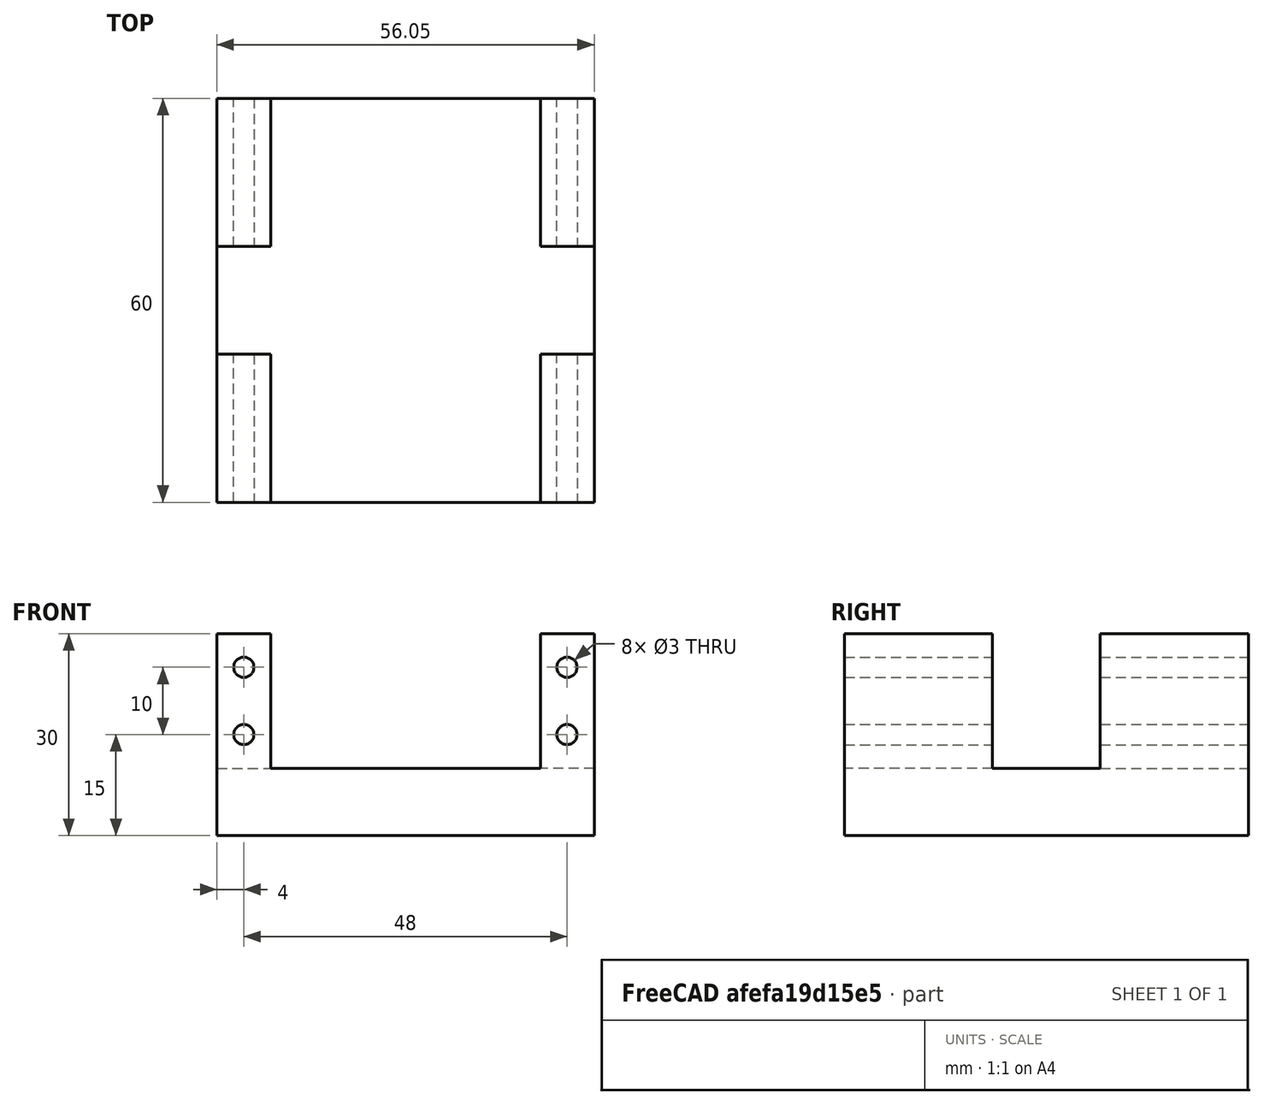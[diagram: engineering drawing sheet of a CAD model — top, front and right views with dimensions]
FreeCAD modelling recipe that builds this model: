
FCSTD DOCUMENT  (FreeCAD 1.0R38806 (Git))
Label: soporte_patas_bien
License: All rights reserved
LicenseURL: https://en.wikipedia.org/wiki/All_rights_reserved
objects: TechDraw::DrawViewDimension×9, TechDraw::DrawProjGroupItem×8, Sketcher::SketchObject×5, PartDesign::Pad×5, Part::Cylinder×4, Part::Cut×4, TechDraw::DrawSVGTemplate×2, TechDraw::DrawProjGroup×2, TechDraw::DrawPage×2, PartDesign::Body×1
note: 51 computed .brp shape members not serialized (recipe doc carries the construction recipe); baked Part::Feature solids carry a one-line shape summary decoded from their .brp

FEATURE [Sketcher::SketchObject] Sketch
  ArcFitTolerance = 1e-06
  AttachmentSupport = -> [XY_Plane]
  FullyConstrained = true
  MakeInternals = false
  MapMode = 5
  sketch-geometry (4):
    g0: LineSegment StartX=0 StartY=0 StartZ=0 EndX=0 EndY=-60 EndZ=0
    g1: LineSegment StartX=0 StartY=-60 StartZ=0 EndX=56.05 EndY=-60 EndZ=0
    g2: LineSegment StartX=56.05 StartY=-60 StartZ=0 EndX=56.05 EndY=0 EndZ=0
    g3: LineSegment StartX=56.05 StartY=0 StartZ=0 EndX=0 EndY=0 EndZ=0
  constraints (11):
    c: Coincident(g-1,g0)
    c: PointOnObject(g0,g-2)
    c: Coincident(g0,g1)
    c: Horizontal(g1)
    c: Coincident(g1,g2)
    c: PointOnObject(g2,g-1)
    c: Vertical(g2)
    c: Coincident(g2,g3)
    c: Coincident(g3,g0)
    c: Distance(g0) = 60
    c: Distance(g3) = 56.05
FEATURE [PartDesign::Pad] Pad
  Direction = (0,0,1)
  Length = 10
  Length2 = 10
  Profile = -> Sketch
  ReferenceAxis = -> Sketch [N_Axis]
  Refine = true
  Suppressed = false
  Type = 0
FEATURE [Sketcher::SketchObject] Sketch003
  ArcFitTolerance = 1e-06
  AttachmentSupport = -> [XY_Plane]
  FullyConstrained = true
  MakeInternals = false
  MapMode = 5
  sketch-geometry (4):
    g0: LineSegment StartX=0 StartY=0 StartZ=0 EndX=8 EndY=0 EndZ=0
    g1: LineSegment StartX=8 StartY=0 StartZ=0 EndX=8 EndY=-22 EndZ=0
    g2: LineSegment StartX=8 StartY=-22 StartZ=0 EndX=0 EndY=-22 EndZ=0
    g3: LineSegment StartX=0 StartY=-22 StartZ=0 EndX=0 EndY=0 EndZ=0
  constraints (11):
    c: Coincident(g-1,g0)
    c: PointOnObject(g0,g-1)
    c: Coincident(g0,g1)
    c: Vertical(g1)
    c: Coincident(g1,g2)
    c: PointOnObject(g2,g-2)
    c: Horizontal(g2)
    c: Coincident(g2,g3)
    c: Coincident(g3,g0)
    c: Distance(g3) = 22
    c: Distance(g0) = 8
FEATURE [PartDesign::Pad] Pad002
  BaseFeature = -> Pad
  Direction = (0,0,1)
  Length = 30
  Length2 = 10
  Profile = -> Sketch003
  ReferenceAxis = -> Sketch003 [N_Axis]
  Refine = true
  Suppressed = false
  Type = 0
FEATURE [Sketcher::SketchObject] Sketch004
  ArcFitTolerance = 1e-06
  AttachmentSupport = -> [XY_Plane]
  FullyConstrained = true
  MakeInternals = false
  MapMode = 5
  sketch-geometry (4):
    g0: LineSegment StartX=48.05 StartY=0 StartZ=0 EndX=48.05 EndY=-22 EndZ=0
    g1: LineSegment StartX=48.05 StartY=-22 StartZ=0 EndX=56.05 EndY=-22 EndZ=0
    g2: LineSegment StartX=56.05 StartY=-22 StartZ=0 EndX=56.05 EndY=0 EndZ=0
    g3: LineSegment StartX=56.05 StartY=0 StartZ=0 EndX=48.05 EndY=0 EndZ=0
  constraints (12):
    c: Vertical(g0)
    c: Coincident(g0,g1)
    c: Horizontal(g1)
    c: Coincident(g1,g2)
    c: PointOnObject(g2,g-1)
    c: Vertical(g2)
    c: Coincident(g2,g3)
    c: Coincident(g3,g0)
    c: Distance(g3) = 8
    c: Distance(g0) = 22
    c: DistanceX(g0,g-1) = -48.05
    c: DistanceY(g0,g-1) = 0
FEATURE [PartDesign::Pad] Pad003
  BaseFeature = -> Pad002
  Direction = (0,0,1)
  Length = 30
  Length2 = 10
  Profile = -> Sketch004
  ReferenceAxis = -> Sketch004 [N_Axis]
  Refine = true
  Suppressed = false
  Type = 0
FEATURE [Sketcher::SketchObject] Sketch005
  ArcFitTolerance = 1e-06
  AttachmentSupport = -> [XY_Plane]
  FullyConstrained = true
  MakeInternals = false
  MapMode = 5
  sketch-geometry (4):
    g0: LineSegment StartX=0 StartY=-60 StartZ=0 EndX=8 EndY=-60 EndZ=0
    g1: LineSegment StartX=8 StartY=-60 StartZ=0 EndX=8 EndY=-38 EndZ=0
    g2: LineSegment StartX=8 StartY=-38 StartZ=0 EndX=0 EndY=-38 EndZ=0
    g3: LineSegment StartX=0 StartY=-38 StartZ=0 EndX=0 EndY=-60 EndZ=0
  constraints (12):
    c: PointOnObject(g0,g-2)
    c: Horizontal(g0)
    c: Coincident(g0,g1)
    c: Vertical(g1)
    c: Distance(g1) = 22
    c: Distance(g0) = 8
    c: Coincident(g2,g1)
    c: Horizontal(g2)
    c: Coincident(g3,g2)
    c: Coincident(g3,g0)
    c: Vertical(g3)
    c: DistanceY(g0,g-1) = 60
FEATURE [PartDesign::Pad] Pad004
  BaseFeature = -> Pad003
  Direction = (0,0,1)
  Length = 30
  Length2 = 10
  Profile = -> Sketch005
  ReferenceAxis = -> Sketch005 [N_Axis]
  Refine = true
  Suppressed = false
  Type = 0
FEATURE [Sketcher::SketchObject] Sketch006
  ArcFitTolerance = 1e-06
  AttachmentSupport = -> [XY_Plane]
  FullyConstrained = true
  MakeInternals = false
  MapMode = 5
  sketch-geometry (4):
    g0: LineSegment StartX=56.05 StartY=-60 StartZ=0 EndX=48.05 EndY=-60 EndZ=0
    g1: LineSegment StartX=48.05 StartY=-60 StartZ=0 EndX=48.05 EndY=-38 EndZ=0
    g2: LineSegment StartX=48.05 StartY=-38 StartZ=0 EndX=56.05 EndY=-38 EndZ=0
    g3: LineSegment StartX=56.05 StartY=-38 StartZ=0 EndX=56.05 EndY=-60 EndZ=0
  constraints (12):
    c: Horizontal(g0)
    c: Coincident(g0,g1)
    c: Vertical(g1)
    c: Coincident(g1,g2)
    c: Horizontal(g2)
    c: Distance(g1) = 22
    c: Distance(g2) = 8
    c: DistanceX(g1,g-1) = -48.05
    c: DistanceY(g1,g-1) = 38
    c: Coincident(g3,g2)
    c: Coincident(g3,g0)
    c: Vertical(g3)
FEATURE [PartDesign::Pad] Pad005
  BaseFeature = -> Pad004
  Direction = (0,0,1)
  Length = 30
  Length2 = 10
  Profile = -> Sketch006
  ReferenceAxis = -> Sketch006 [N_Axis]
  Refine = true
  Suppressed = false
  Type = 0
FEATURE [PartDesign::Body] Body
  AllowCompound = false
  Group = -> [Sketch,Pad,Sketch003,Pad002,Sketch004,Pad003,Sketch005,Pad004,Sketch006,Pad005]
  Origin = -> Origin
  Tip = -> Pad005
FEATURE [Part::Cylinder] Cylinder
  Angle = 360
  AttacherType = Attacher::AttachEngine3D
  FirstAngle = 0
  Height = 60
  Placement = pos=(4,0,25) rot=(1,0,0;1.5708rad)
  Radius = 1.5
  SecondAngle = 0
FEATURE [Part::Cylinder] Cylinder001
  Angle = 360
  AttacherType = Attacher::AttachEngine3D
  FirstAngle = 0
  Height = 60
  Placement = pos=(4,0,15) rot=(1,0,0;1.5708rad)
  Radius = 1.5
  SecondAngle = 0
FEATURE [Part::Cylinder] Cylinder002
  Angle = 360
  AttacherType = Attacher::AttachEngine3D
  FirstAngle = 0
  Height = 60
  Placement = pos=(52,0,25) rot=(1,0,0;1.5708rad)
  Radius = 1.5
  SecondAngle = 0
FEATURE [Part::Cylinder] Cylinder003
  Angle = 360
  AttacherType = Attacher::AttachEngine3D
  FirstAngle = 0
  Height = 60
  Placement = pos=(52,0,15) rot=(1,0,0;1.5708rad)
  Radius = 1.5
  SecondAngle = 0
FEATURE [Part::Cut] Cut
  Base = -> Body
  Refine = true
  Tool = -> Cylinder
FEATURE [Part::Cut] Cut001
  Base = -> Cut
  Refine = true
  Tool = -> Cylinder001
FEATURE [Part::Cut] Cut002
  Base = -> Cut001
  Refine = true
  Tool = -> Cylinder002
FEATURE [Part::Cut] Cut003
  Base = -> Cut002
  Refine = true
  Tool = -> Cylinder003
FEATURE [TechDraw::DrawSVGTemplate] Template
  Height = 210
  Orientation = 1
  Template = <path>
  Width = 297
FEATURE [TechDraw::DrawProjGroupItem] View  label="Front"
  CoarseView = false
  Direction = (0,-1,0)
  Focus = 100
  HardHidden = false
  IsoCount = 0
  IsoHidden = false
  IsoVisible = false
  LockPosition = true
  Perspective = false
  Rotation = 0
  RotationVector = (1,0,0)
  ScaleType = 2
  ScrubCount = 1
  SeamHidden = false
  SeamVisible = false
  SmoothHidden = false
  SmoothVisible = true
  Source = -> [Cut003]
  Type = 0
  X = 0
  XDirection = (1,0,0)
  Y = 0
FEATURE [TechDraw::DrawProjGroupItem] ProjItem  label="FrontTopRight"
  CoarseView = false
  Direction = (0.57735,-0.57735,0.57735)
  Focus = 100
  HardHidden = false
  IsoCount = 0
  IsoHidden = false
  IsoVisible = false
  LockPosition = false
  Perspective = false
  Rotation = 0
  RotationVector = (1,0,0)
  ScaleType = 0
  ScrubCount = 1
  SeamHidden = false
  SeamVisible = false
  SmoothHidden = false
  SmoothVisible = true
  Source = -> [Cut003]
  Type = 7
  X = -84.0549
  XDirection = (0.707107,0.707107,0)
  Y = -65.9361
FEATURE [TechDraw::DrawProjGroupItem] ProjItem002  label="Right"
  CoarseView = false
  Direction = (1,-1e-16,0)
  Focus = 100
  HardHidden = false
  IsoCount = 0
  IsoHidden = false
  IsoVisible = false
  LockPosition = false
  Perspective = false
  Rotation = 0
  RotationVector = (1,0,0)
  ScaleType = 0
  ScrubCount = 1
  SeamHidden = false
  SeamVisible = false
  SmoothHidden = false
  SmoothVisible = true
  Source = -> [Cut003]
  Type = 2
  X = -84.0549
  XDirection = (1e-16,1,0)
  Y = 0
FEATURE [TechDraw::DrawProjGroupItem] ProjItem003  label="Top"
  CoarseView = false
  Direction = (0,0,1)
  Focus = 100
  HardHidden = false
  IsoCount = 0
  IsoHidden = false
  IsoVisible = false
  LockPosition = false
  Perspective = false
  Rotation = 0
  RotationVector = (1,0,0)
  ScaleType = 0
  ScrubCount = 1
  SeamHidden = false
  SeamVisible = false
  SmoothHidden = false
  SmoothVisible = true
  Source = -> [Cut003]
  Type = 4
  X = 0
  XDirection = (1,0,0)
  Y = -65.9361
FEATURE [TechDraw::DrawProjGroup] ProjGroup
  Anchor = -> View
  AutoDistribute = true
  LockPosition = false
  ProjectionType = 0
  Rotation = 0
  ScaleType = 0
  Source = -> [Cut003]
  Views = -> [View,ProjItem,ProjItem002,ProjItem003]
  X = 123.085
  Y = 167.67
  spacingX = 15
  spacingY = 15
FEATURE [TechDraw::DrawViewDimension] Dimension
  AngleOverride = false
  Arbitrary = false
  ArbitraryTolerances = false
  BoxCorners = (2) [(-28.025,-30,0),(28.025,30,0)]
  EqualTolerance = true
  ExtensionAngle = 0
  FormatSpec = %.2w
  FormatSpecOverTolerance = %+.2w
  FormatSpecUnderTolerance = %+.2w
  Inverted = false
  LineAngle = 0
  LockPosition = false
  MeasureType = 1
  OverTolerance = 0
  References2D = -> [ProjItem003]
  Rotation = 0
  ScaleType = 0
  TheoreticalExact = false
  Type = 1
  UnderTolerance = 0
  X = 0
  Y = -41.7363
FEATURE [TechDraw::DrawViewDimension] Dimension001
  AngleOverride = false
  Arbitrary = false
  ArbitraryTolerances = false
  BoxCorners = (2) [(-30,-15,0),(30,15,0)]
  EqualTolerance = true
  ExtensionAngle = 0
  FormatSpec = %.2w
  FormatSpecOverTolerance = %+.2w
  FormatSpecUnderTolerance = %+.2w
  Inverted = false
  LineAngle = 0
  LockPosition = false
  MeasureType = 1
  OverTolerance = 0
  References2D = -> [ProjItem002]
  Rotation = 0
  ScaleType = 0
  TheoreticalExact = false
  Type = 1
  UnderTolerance = 0
  X = 0
  Y = -28.2519
FEATURE [TechDraw::DrawViewDimension] Dimension002
  AngleOverride = false
  Arbitrary = false
  ArbitraryTolerances = false
  BoxCorners = (2) [(-28.025,-30,0),(28.025,30,0)]
  EqualTolerance = true
  ExtensionAngle = 0
  FormatSpec = %.2w
  FormatSpecOverTolerance = %+.2w
  FormatSpecUnderTolerance = %+.2w
  Inverted = false
  LineAngle = 0
  LockPosition = false
  MeasureType = 1
  OverTolerance = 0
  References2D = -> [ProjItem003]
  Rotation = 0
  ScaleType = 0
  TheoreticalExact = false
  Type = 2
  UnderTolerance = 0
  X = -39.8527
  Y = 19
FEATURE [TechDraw::DrawViewDimension] Dimension003
  AngleOverride = false
  Arbitrary = false
  ArbitraryTolerances = false
  BoxCorners = (2) [(-28.025,-15,0),(28.025,15,0)]
  EqualTolerance = true
  ExtensionAngle = 0
  FormatSpec = %.2w
  FormatSpecOverTolerance = %+.2w
  FormatSpecUnderTolerance = %+.2w
  Inverted = false
  LineAngle = 0
  LockPosition = false
  MeasureType = 1
  OverTolerance = 0
  References2D = -> [View]
  Rotation = 0
  ScaleType = 0
  TheoreticalExact = false
  Type = 1
  UnderTolerance = 0
  X = -24.025
  Y = 30.9524
FEATURE [TechDraw::DrawPage] Page
  KeepUpdated = true
  NextBalloonIndex = 1
  ProjectionType = 0
  Template = -> Template
  Views = -> [ProjGroup,Dimension,Dimension001,Dimension002,Dimension003]
FEATURE [TechDraw::DrawSVGTemplate] Template001
  EditableTexts = approval_person=Mecatrónica; creator=A.Mrtz, N.Grc, TMari; date_of_issue=12/15/24; document_status=In preparation; document_type=Assembly Drawing; drawing_number=DN; general_tolerances=ISO 2768-m; language_code=EN; part_material=Stainless steel Mat.No. 1.4301; responsible_department=RD; revision_index=AAA; sheet_number=2 / 2; sheet_scale=1 : 1; title=Soporte patas
  Height = 297
  Orientation = 1
  Template = <path>
  Width = 420
FEATURE [TechDraw::DrawProjGroupItem] View001  label="Front001"
  CoarseView = false
  Direction = (0,-1,0)
  Focus = 100
  HardHidden = false
  IsoCount = 0
  IsoHidden = false
  IsoVisible = false
  LockPosition = true
  Perspective = false
  Rotation = 0
  RotationVector = (1,0,0)
  Scale = 1.5
  ScaleType = 2
  ScrubCount = 1
  SeamHidden = false
  SeamVisible = false
  SmoothHidden = false
  SmoothVisible = true
  Source = -> [Cut003]
  Type = 0
  X = 0
  XDirection = (1,0,0)
  Y = 0
FEATURE [TechDraw::DrawProjGroupItem] ProjItem004  label="FrontTopRight001"
  CoarseView = false
  Direction = (0.57735,-0.57735,0.57735)
  Focus = 100
  HardHidden = false
  IsoCount = 0
  IsoHidden = false
  IsoVisible = false
  LockPosition = false
  Perspective = false
  Rotation = 0
  RotationVector = (1,0,0)
  Scale = 1.5
  ScaleType = 2
  ScrubCount = 1
  SeamHidden = false
  SeamVisible = false
  SmoothHidden = false
  SmoothVisible = true
  Source = -> [Cut003]
  Type = 7
  X = 133.871
  XDirection = (0.707107,0.707107,0)
  Y = -15.3965
FEATURE [TechDraw::DrawProjGroupItem] ProjItem005  label="Top001"
  CoarseView = false
  Direction = (0,0,1)
  Focus = 100
  HardHidden = false
  IsoCount = 0
  IsoHidden = false
  IsoVisible = false
  LockPosition = false
  Perspective = false
  Rotation = 0
  RotationVector = (1,0,0)
  Scale = 1.5
  ScaleType = 2
  ScrubCount = 1
  SeamHidden = false
  SeamVisible = false
  SmoothHidden = false
  SmoothVisible = true
  Source = -> [Cut003]
  Type = 4
  X = 0
  XDirection = (1,0,0)
  Y = -110.406
FEATURE [TechDraw::DrawProjGroupItem] ProjItem006  label="Right001"
  CoarseView = false
  Direction = (1,-1e-16,0)
  Focus = 100
  HardHidden = false
  IsoCount = 0
  IsoHidden = false
  IsoVisible = false
  LockPosition = false
  Perspective = false
  Rotation = 0
  RotationVector = (1,0,0)
  Scale = 1.5
  ScaleType = 2
  ScrubCount = 1
  SeamHidden = false
  SeamVisible = false
  SmoothHidden = false
  SmoothVisible = true
  Source = -> [Cut003]
  Type = 2
  X = -118.582
  XDirection = (1e-16,1,0)
  Y = 0
FEATURE [TechDraw::DrawProjGroup] ProjGroup001
  Anchor = -> View001
  AutoDistribute = true
  LockPosition = false
  ProjectionType = 0
  Rotation = 0
  Scale = 1.5
  ScaleType = 1
  Source = -> [Cut003]
  Views = -> [View001,ProjItem004,ProjItem005,ProjItem006]
  X = 202.094
  Y = 232.081
  spacingX = 15
  spacingY = 15
FEATURE [TechDraw::DrawViewDimension] Dimension004
  AngleOverride = false
  Arbitrary = false
  ArbitraryTolerances = false
  BoxCorners = (2) [(-30,-15,0),(30,15,0)]
  EqualTolerance = true
  ExtensionAngle = 0
  FormatSpec = %.2w
  FormatSpecOverTolerance = %+.2w
  FormatSpecUnderTolerance = %+.2w
  Inverted = false
  LineAngle = 0
  LockPosition = false
  MeasureType = 1
  OverTolerance = 0
  References2D = -> [ProjItem006]
  Rotation = 0
  ScaleType = 0
  TheoreticalExact = false
  Type = 1
  UnderTolerance = 0
  X = 0
  Y = -31.3507
FEATURE [TechDraw::DrawViewDimension] Dimension005
  AngleOverride = false
  Arbitrary = false
  ArbitraryTolerances = false
  BoxCorners = (2) [(-28.025,-15,0),(28.025,15,0)]
  EqualTolerance = true
  ExtensionAngle = 0
  FormatSpec = %.2w
  FormatSpecOverTolerance = %+.2w
  FormatSpecUnderTolerance = %+.2w
  Inverted = false
  LineAngle = 0
  LockPosition = false
  MeasureType = 1
  OverTolerance = 0
  References2D = -> [View001]
  Rotation = 0
  ScaleType = 0
  TheoreticalExact = false
  Type = 1
  UnderTolerance = 0
  X = 0
  Y = -32.8566
FEATURE [TechDraw::DrawViewDimension] Dimension006
  AngleOverride = false
  Arbitrary = false
  ArbitraryTolerances = false
  BoxCorners = (2) [(-28.025,-30,0),(28.025,30,0)]
  EqualTolerance = true
  ExtensionAngle = 0
  FormatSpec = %.2w
  FormatSpecOverTolerance = %+.2w
  FormatSpecUnderTolerance = %+.2w
  Inverted = false
  LineAngle = 0
  LockPosition = false
  MeasureType = 1
  OverTolerance = 0
  References2D = -> [ProjItem005]
  Rotation = 0
  ScaleType = 0
  TheoreticalExact = false
  Type = 1
  UnderTolerance = 0
  X = -36.0375
  Y = 62.0691
FEATURE [TechDraw::DrawViewDimension] Dimension007
  AngleOverride = false
  Arbitrary = false
  ArbitraryTolerances = false
  BoxCorners = (2) [(-42.0375,-45,0),(42.0375,45,0)]
  EqualTolerance = true
  ExtensionAngle = 0
  FormatSpec = %.2w
  FormatSpecOverTolerance = %+.2w
  FormatSpecUnderTolerance = %+.2w
  Inverted = false
  LineAngle = 0
  LockPosition = false
  MeasureType = 1
  OverTolerance = 0
  References2D = -> [ProjItem005]
  Rotation = 0
  ScaleType = 0
  TheoreticalExact = false
  Type = 2
  UnderTolerance = 0
  X = -60.3987
  Y = 28.5
FEATURE [TechDraw::DrawViewDimension] Dimension008
  AngleOverride = false
  Arbitrary = false
  ArbitraryTolerances = false
  BoxCorners = (2) [(-42.0375,-22.5,0),(42.0375,22.5,0)]
  EqualTolerance = true
  ExtensionAngle = 0
  FormatSpec = ⌀%.2w
  FormatSpecOverTolerance = %+.2w
  FormatSpecUnderTolerance = %+.2w
  Inverted = false
  LineAngle = 0
  LockPosition = false
  MeasureType = 1
  OverTolerance = 0
  References2D = -> [View001]
  Rotation = 0
  ScaleType = 0
  TheoreticalExact = false
  Type = 5
  UnderTolerance = 0
  X = -21.2734
  Y = 29.2922
FEATURE [TechDraw::DrawPage] Page001
  KeepUpdated = true
  NextBalloonIndex = 1
  ProjectionType = 0
  Template = -> Template001
  Views = -> [ProjGroup001,Dimension004,Dimension005,Dimension006,Dimension007,Dimension008]
note: 2 file-system paths scrubbed to <path> (originals preserved in the JSON sidecar)
